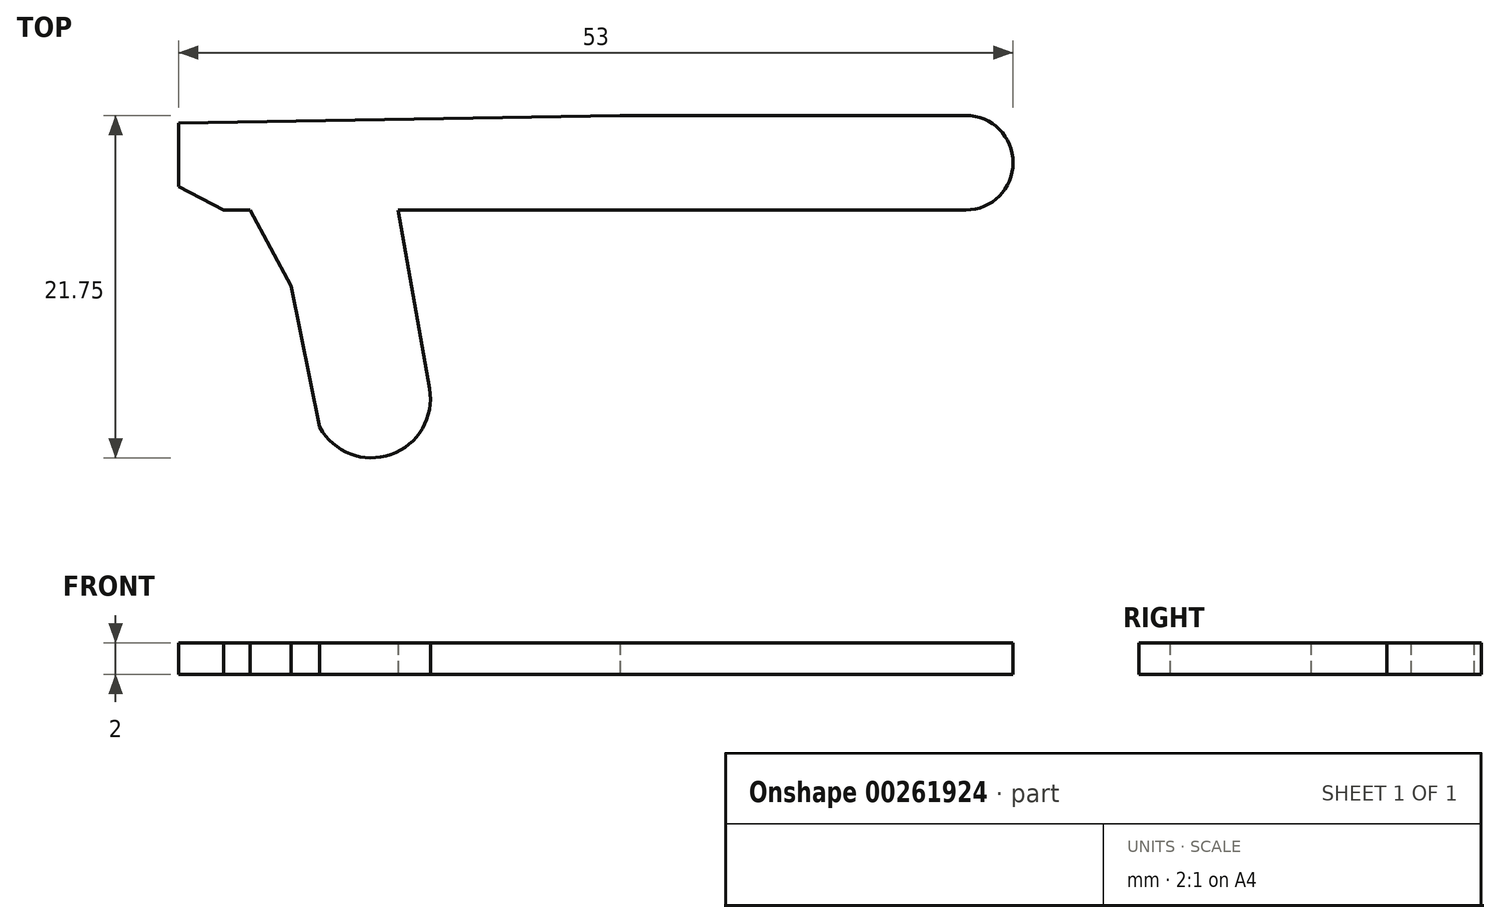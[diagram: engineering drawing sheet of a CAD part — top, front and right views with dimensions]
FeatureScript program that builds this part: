
annotation { "Feature Type Name" : "Feature", "Feature Type Description" : "" }
export const myFeature = defineFeature(function(context is Context, id is Id, definition is map)
    precondition{}
    {
        {
            var Q0;
            Q0=qCreatedBy(makeId("Top.planeOp"),FACE);
            var sketch = newSketch(context, id + "F0", { "sketchPlane" : qUnion([Q0])});
            skLineSegment(sketch, "E0", {"start": v(41.04, 14.85) * mm, "end": v(19.07, 14.85) * mm});
            skLineSegment(sketch, "E1", {"start": v(19.07, 14.85) * mm, "end": v(-8.96, 14.37) * mm});
            skLineSegment(sketch, "E2", {"start": v(6.97, -2.5) * mm, "end": v(4.97, 8.85) * mm});
            skLineSegment(sketch, "E3", {"start": v(4.97, 8.85) * mm, "end": v(41.04, 8.85) * mm});
            skArc(sketch, "E4", {"start": v(6.97, -2.5) * mm, "mid": v(4.53, -6.68) * mm, "end": v(0, -4.95) * mm});
            skArc(sketch, "E5", {"start": v(41.04, 8.85) * mm, "mid": v(44.04, 11.85) * mm, "end": v(41.04, 14.85) * mm});
            skLineSegment(sketch, "E6", {"start": v(-6.12, 8.85) * mm, "end": v(-4.43, 8.85) * mm});
            skLineSegment(sketch, "E7", {"start": v(0, -4.95) * mm, "end": v(-1.83, 4.02) * mm});
            skLineSegment(sketch, "E8", {"start": v(-1.83, 4.02) * mm, "end": v(-4.43, 8.85) * mm});
            skLineSegment(sketch, "E9", {"start": v(-6.12, 8.85) * mm, "end": v(-8.96, 10.35) * mm});
            skLineSegment(sketch, "E10", {"start": v(-8.96, 10.35) * mm, "end": v(-8.96, 14.37) * mm});
            skSolve(sketch);
        }
        {
            var Q0;
            Q0=makeQuery(id+"F0.imprint","IMPRINT",FACE,{"disambiguationData":[TD([[makeQuery(id+"F0.imprint","IMPRINT",EDGE,{"derivedFrom":sQuery(id+"F0.wireOp",EDGE,"E0")}),1.0]])]});
            extrude(context, id + "F1", {"entities" : qUnion([Q0]), "depth" : 2 * mm});
        }
    });
